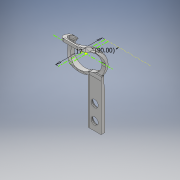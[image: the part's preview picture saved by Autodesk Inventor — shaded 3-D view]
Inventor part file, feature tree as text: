
AUTODESK INVENTOR PART (.ipt)
format: ipt  version: 2018 (Build 220112000, 112)  size: 5,239,808 bytes
history: native  units: mm
features: sketch x154, extrude x143, fillet x57, hole x4, direct_edit x3, mirror x3, other x3
ambient origin geometry x8: Origin, YZ Plane, XZ Plane, XY Plane, X Axis, Y Axis, Z Axis, Center Point
bodies: Solid2 (feature_tree)
feature tree (367):
  extrude  "Extrusion15"  Depth=18.0mm
  extrude  "Extrusion16"  Depth=1.0mm TaperAngle=0.0deg
  sketch  "Sketch28"  dims[d118=18.7mm d119=0.0mm d120=0.9mm d121=0.0mm]
  extrude  "Extrusion21"  Depth=0.9mm TaperAngle=0.0deg
  extrude  "Extrusion22"  Depth=3.467mm
  extrude  "Extrusion23"  Depth=46.7mm
  hole  "Hole6"  [1 undecoded]
  extrude  "Extrusion27"  Depth=3.467mm
  extrude  "Extrusion28"  Depth=32.03mm
  extrude  "Extrusion30"  Depth=10.0mm TaperAngle=0.0deg
  extrude  "Extrusion31"  Depth=10.0mm
  direct_edit  "Direct Edit1"
  sketch  "Sketch56"  dims[d186=16.3mm d187=0.0mm d188=16.3mm d189=0.0mm]
  sketch  "Sketch57"  dims[d190=16.3mm d191=0.0mm d192=16.3mm d193=0.0mm]
  extrude  "Extrusion33"  Depth=16.3mm TaperAngle=0.0deg
  extrude  "Extrusion34"  Depth=16.3mm TaperAngle=0.0deg
  extrude  "Extrusion35"  Depth=15.9mm TaperAngle=0.0deg
  extrude  "Extrusion36"  Depth=15.9mm TaperAngle=0.0deg
  extrude  "Extrusion37"  Depth=17.0mm
  extrude  "Extrusion38"  Depth=6.0mm TaperAngle=0.0deg
  extrude  "Extrusion39"  Depth=6.0mm TaperAngle=0.0deg
  extrude  "Extrusion40"  Depth=3.17mm
  extrude  "Extrusion41"  Depth=19.4mm
  sketch  "Sketch68"  dims[d249=0.0mm d250=0.0mm d251=10.0mm d252=0.0mm]
  sketch  "Sketch69"  dims[d253=3.91mm d254=0.0mm d255=0.0mm d256=0.0mm]
  extrude  "Extrusion42"  Depth=0.8mm TaperAngle=0.0deg
  extrude  "Extrusion43"  Depth=10.0mm
  extrude  "Extrusion45"  Depth=10.0mm TaperAngle=0.0deg
  extrude  "Extrusion47"  TaperAngle=0.0deg  [1 undecoded]
  extrude  "Extrusion48"  Depth=10.0mm TaperAngle=0.0deg
  extrude  "Extrusion49"  Depth=0.6mm TaperAngle=0.0deg
  direct_edit  "Direct Edit3"
  extrude  "Extrusion51"  Depth=0.199mm
  extrude  "Extrusion52"  TaperAngle=0.0deg  [1 undecoded]
  extrude  "Extrusion53"  Depth=0.7mm TaperAngle=0.0deg
  extrude  "Extrusion54"  Depth=3.64mm
  extrude  "Extrusion55"  Depth=0.09mm TaperAngle=0.0deg
  extrude  "Extrusion57"  Depth=0.356mm
  extrude  "Extrusion60"  Depth=3.9mm TaperAngle=0.0deg
  extrude  "Extrusion61"  Depth=3.9mm TaperAngle=0.0deg
  extrude  "Extrusion62"  Depth=0.886mm
  fillet  "Fillet13"  Radius=3.9mm
  extrude  "Extrusion63"  Depth=10.0mm TaperAngle=0.0deg
  extrude  "Extrusion64"  TaperAngle=0.0deg  [1 undecoded]
  extrude  "Extrusion65"  TaperAngle=0.0deg  [1 undecoded]
  extrude  "Extrusion66"  Depth=0.253mm
  extrude  "Extrusion67"  TaperAngle=0.0deg  [1 undecoded]
  fillet  "Fillet14"  [1 undecoded]
  extrude  "Extrusion68"  Depth=15.0mm
  extrude  "Extrusion69"  Depth=22.68928mm
  extrude  "Extrusion70"  TaperAngle=90.0deg  [1 undecoded]
  fillet  "Fillet15"  [1 undecoded]
  extrude  "Extrusion71"  Depth=0.954mm
  extrude  "Extrusion72"  Depth=3.490659mm
  extrude  "Extrusion73"  Depth=6.0mm TaperAngle=0.0deg
  extrude  "Extrusion74"  Depth=2.0mm TaperAngle=0.0deg
  fillet  "Fillet16"  Radius=2.0mm
  fillet  "Fillet17"  [1 undecoded]
  extrude  "Extrusion75"  Depth=10.0mm
  extrude  "Extrusion77"  Depth=5.0mm TaperAngle=0.0deg
  extrude  "Extrusion78"  Depth=3.8mm
  extrude  "Extrusion79"  Depth=3.213mm
  extrude  "Extrusion80"  Depth=10.0mm TaperAngle=0.0deg
  extrude  "Extrusion81"  Depth=10.0mm TaperAngle=0.0deg
  extrude  "Extrusion82"  Depth=10.0mm TaperAngle=0.0deg
  fillet  "Fillet18"  Radius=10.0mm
  fillet  "Fillet19"  Radius=10.0mm
  fillet  "Fillet20"  Radius=10.0mm
  extrude  "Extrusion83"  Depth=10.0mm TaperAngle=0.0deg
  extrude  "Extrusion84"  TaperAngle=0.0deg  [1 undecoded]
  extrude  "Extrusion85"  Depth=1.49mm
  fillet  "Fillet21"  Radius=0.859mm
  extrude  "Extrusion87"  Depth=0.149mm
  extrude  "Extrusion88"  Depth=1.77mm
  extrude  "Extrusion89"  Depth=10.0mm TaperAngle=0.0deg
  direct_edit  "Direct Edit7"
  extrude  "Extrusion90"  Depth=4.0mm TaperAngle=0.0deg
  extrude  "Extrusion91"  TaperAngle=0.0deg  [1 undecoded]
  fillet  "Fillet27"  [1 undecoded]
  extrude  "Extrusion92"  Depth=7.0mm TaperAngle=0.0deg
  extrude  "Extrusion93"  Depth=10.0mm TaperAngle=0.0deg
  extrude  "Extrusion94"  Depth=7.0mm TaperAngle=0.0deg
  fillet  "Fillet29"  Radius=7.0mm
  hole  "Hole7"  [1 undecoded]
  extrude  "Extrusion95"  Depth=1.7mm TaperAngle=0.0deg
  extrude  "Extrusion97"  Depth=8.713mm
  extrude  "Extrusion98"  Depth=2.6mm
  extrude  "Extrusion99"  TaperAngle=0.0deg  [1 undecoded]
  extrude  "Extrusion100"  Depth=10.0mm TaperAngle=0.0deg
  extrude  "Extrusion101"  Depth=10.0mm TaperAngle=0.0deg
  extrude  "Extrusion102"  TaperAngle=0.0deg  [1 undecoded]
  extrude  "Extrusion103"  Depth=10.0mm TaperAngle=0.0deg
  extrude  "Extrusion104"  TaperAngle=0.0deg  [1 undecoded]
  extrude  "Extrusion105"  Depth=1.64mm
  fillet  "Fillet30"  Radius=0.5mm
  extrude  "Extrusion106"  TaperAngle=0.0deg  [1 undecoded]
  fillet  "Fillet33"  Radius=1.2mm
  fillet  "Fillet34"  Radius=1.2mm
  fillet  "Fillet35"  Radius=1.29mm
  extrude  "Extrusion107"  Depth=10.0mm TaperAngle=0.0deg
  fillet  "Fillet36"  Radius=4.668mm
  fillet  "Fillet37"  Radius=1.4mm
  fillet  "Fillet38"  Radius=25.3mm
  extrude  "Extrusion108"  TaperAngle=0.0deg  [1 undecoded]
  extrude  "Extrusion109"  Depth=25.3mm TaperAngle=0.0deg
  extrude  "Extrusion110"  Depth=0.25mm TaperAngle=0.0deg
  extrude  "Extrusion111"  Depth=2.0mm
  extrude  "Extrusion112"  Depth=2.01mm
  sketch  "Sketch146"  dims[d552=0.25mm d553=0.0mm d554=1.4mm d555=0.0mm]
  extrude  "Extrusion113"  Depth=1.4mm TaperAngle=0.0deg
  extrude  "Extrusion114"  Depth=2.0mm
  extrude  "Extrusion115"  Depth=6.2mm TaperAngle=0.0deg
  extrude  "Extrusion116"  Depth=2.0mm
  extrude  "Extrusion118"  Depth=6.2mm TaperAngle=0.0deg
  sketch  "Sketch154"  dims[d573=5.5mm d574=2.334mm]
  extrude  "Extrusion119"  Depth=2.6mm
  extrude  "Extrusion120"  Depth=2.334mm
  extrude  "Extrusion121"  Depth=3.213mm
  extrude  "Extrusion122"  Depth=10.0mm TaperAngle=0.0deg
  extrude  "Extrusion123"  Depth=2.0mm
  extrude  "Extrusion124"  Depth=10.0mm
  extrude  "Extrusion125"  Depth=12.8mm
  extrude  "Extrusion126"  Depth=10.0mm TaperAngle=0.0deg
  extrude  "Extrusion127"  Depth=8.47mm
  hole  "Hole8"  [1 undecoded]
  extrude  "Extrusion128"  Depth=3.2mm TaperAngle=0.0deg
  extrude  "Extrusion129"  Depth=2.0mm
  extrude  "Extrusion130"  Depth=2.0mm
  extrude  "Extrusion132"  Depth=2.0mm TaperAngle=0.0deg
  extrude  "Extrusion133"  Depth=9.5mm TaperAngle=0.0deg
  extrude  "Extrusion134"  Depth=2.0mm
  extrude  "Extrusion135"  Depth=10.0mm TaperAngle=0.0deg
  extrude  "Extrusion136"  Depth=4.0mm TaperAngle=0.0deg
  extrude  "Extrusion137"  Depth=1.245mm TaperAngle=0.0deg
  extrude  "Extrusion138"  Depth=2.0mm
  extrude  "Extrusion139"  Depth=1.0mm TaperAngle=0.0deg
  extrude  "Extrusion140"  Depth=2.0mm
  sketch  "Sketch182"  dims[d641=1.33mm d642=2.0mm]
  fillet  "Fillet39"  Radius=1.0mm
  extrude  "Extrusion141"  Depth=2.0mm
  extrude  "Extrusion142"  Depth=2.0mm
  sketch  "Sketch185"  dims[d21=1.0mm d22=1.0mm]
  extrude  "Extrusion143"  Depth=2.0mm
  extrude  "Extrusion144"  Depth=2.0mm
  extrude  "Extrusion145"  Depth=1.0mm
  fillet  "Fillet41"  [1 undecoded]
  extrude  "Extrusion146"  [1 undecoded]
  extrude  "Extrusion147"  [1 undecoded]
  extrude  "Extrusion148"  [1 undecoded]
  extrude  "Extrusion149"  [1 undecoded]
  extrude  "Extrusion150"  [1 undecoded]
  extrude  "Extrusion152"  [1 undecoded]
  extrude  "Extrusion153"  [1 undecoded]
  extrude  "Extrusion154"  [1 undecoded]
  extrude  "Extrusion155"  [1 undecoded]
  fillet  "Fillet42"  [1 undecoded]
  fillet  "Fillet43"  [1 undecoded]
  fillet  "Fillet44"  [1 undecoded]
  fillet  "Fillet45"  [1 undecoded]
  extrude  "Extrusion156"  [1 undecoded]
  extrude  "Extrusion157"  [1 undecoded]
  fillet  "Fillet46"  [1 undecoded]
  fillet  "Fillet47"  [1 undecoded]
  fillet  "Fillet48"  [1 undecoded]
  extrude  "Extrusion158"  [1 undecoded]
  extrude  "Extrusion159"  [1 undecoded]
  fillet  "Fillet49"  [1 undecoded]
  extrude  "Extrusion160"  [1 undecoded]
  extrude  "Extrusion162"  [1 undecoded]
  hole  "Hole9"  [1 undecoded]
  sketch  "Sketch205"
  extrude  "Extrusion163"  [1 undecoded]
  fillet  "Fillet50"  [1 undecoded]
  fillet  "Fillet51"  [1 undecoded]
  extrude  "Extrusion164"  [1 undecoded]
  fillet  "Fillet52"  [1 undecoded]
  fillet  "Fillet53"  [1 undecoded]
  fillet  "Fillet54"  [1 undecoded]
  fillet  "Fillet55"  [1 undecoded]
  extrude  "Extrusion165"  [1 undecoded]
  fillet  "Fillet56"  [1 undecoded]
  fillet  "Fillet57"  [1 undecoded]
  extrude  "Extrusion166"  [1 undecoded]
  extrude  "Extrusion167"  [1 undecoded]
  extrude  "Extrusion168"  [1 undecoded]
  extrude  "Extrusion169"  [1 undecoded]
  fillet  "Fillet58"  [1 undecoded]
  fillet  "Fillet59"  [1 undecoded]
  fillet  "Fillet60"  [1 undecoded]
  fillet  "Fillet61"  [1 undecoded]
  fillet  "Fillet62"  [1 undecoded]
  extrude  "Extrusion170"  [1 undecoded]
  extrude  "Extrusion171"  [1 undecoded]
  extrude  "Extrusion172"  [1 undecoded]
  fillet  "Fillet63"  [1 undecoded]
  fillet  "Fillet64"  [1 undecoded]
  fillet  "Fillet65"  [1 undecoded]
  sketch  "Sketch220"
  extrude  "Extrusion173"  [1 undecoded]
  extrude  "Extrusion174"  [1 undecoded]
  extrude  "Extrusion175"  [1 undecoded]
  extrude  "Extrusion176"  [1 undecoded]
  extrude  "Extrusion177"  [1 undecoded]
  fillet  "Fillet66"  [1 undecoded]
  sketch  "Sketch225"
  fillet  "Fillet67"  [1 undecoded]
  fillet  "Fillet68"  [1 undecoded]
  extrude  "Extrusion178"  [1 undecoded]
  fillet  "Fillet69"  [1 undecoded]
  fillet  "Fillet70"  [1 undecoded]
  extrude  "Extrusion179"  [1 undecoded]
  fillet  "Fillet71"  [1 undecoded]
  fillet  "Fillet72"  [1 undecoded]
  fillet  "Fillet73"  [1 undecoded]
  fillet  "Fillet74"  [1 undecoded]
  fillet  "Fillet75"  [1 undecoded]
  fillet  "Fillet76"  [1 undecoded]
  fillet  "Fillet77"  [1 undecoded]
  fillet  "Fillet78"  [1 undecoded]
  mirror  "Mirror7"
  mirror  "Mirror8"
  mirror  "Mirror9"
  sketch  "Sketch26"  dims[d95=7.5mm d96=18.0mm]
  sketch  "Sketch27"  dims[d97=2.3mm d98=0.0mm d101=1.0mm d102=0.0mm]
  sketch  "Sketch41"  dims[d122=0.7mm d123=0.0mm d128=3.467mm]
  sketch  "Sketch42"  dims[d129=3.467mm d130=46.7mm]
  sketch  "Sketch43"  dims[d134=3.467mm d135=4.369mm d136=5.824mm d137=2.0mm d138=14.3117mm d139=6.637mm d140=0.0mm d150=1.5mm d151=0.0mm]
  sketch  "Sketch50"  dims[d152=1.2mm d153=0.0mm d159=3.467mm]
  sketch  "Sketch51"  dims[d161=3.467mm d168=23.3333mm d173=32.03mm]
  sketch  "Sketch53"  dims[d174=16.015mm d175=10.0mm d176=0.0mm]
  sketch  "Sketch54"  dims[d179=0.0mm d180=0.0mm d181=7.5mm d182=10.0mm d183=10.0mm]
  sketch  "Sketch58"  dims[d194=16.3mm d195=0.0mm d196=15.9mm d197=0.0mm]
  sketch  "Sketch60"  dims[d198=15.9mm d199=0.0mm d200=15.9mm d201=0.0mm]
  sketch  "Sketch61"  dims[d202=15.9mm d203=0.0mm d209=17.0mm]
  sketch  "Sketch62"  dims[d210=90.0deg d211=6.0mm d212=0.0mm]
  sketch  "Sketch63"  dims[d213=0.0mm d214=0.0mm d225=6.0mm d226=0.0mm]
  sketch  "Sketch64"  dims[d230=0.2mm d231=0.0mm d232=3.17mm]
  sketch  "Sketch65"  dims[d233=3.17mm d235=19.4mm]
  sketch  "Sketch66"  dims[d236=6.1mm d237=0.8mm d238=0.0mm]
  sketch  "Sketch67"  dims[d239=0.8mm d240=0.0mm d246=9.0mm d247=10.0mm d248=10.0mm]
  sketch  "Sketch70"  dims[d257=3.91mm d258=0.0mm d261=10.0mm d262=0.0mm]
  sketch  "Sketch72"  dims[d267=0.0mm d268=0.0mm d269=0.6mm d270=0.0mm]
  sketch  "Sketch74"  dims[d271=0.0mm d272=0.0mm d273=0.199mm]
  sketch  "Sketch75"  dims[d274=0.7mm d275=0.0mm d276=0.0mm d277=0.0mm]
  sketch  "Sketch76"  dims[d278=0.0mm d279=0.0mm d280=0.7mm d281=0.0mm]
  sketch  "Sketch79"  dims[d282=0.7mm d283=0.0mm d284=3.64mm]
  sketch  "Sketch80"  dims[d285=0.09mm d286=0.0mm d287=0.09mm d288=0.0mm]
  sketch  "Sketch81"  dims[d289=0.0mm d290=0.0mm d291=0.356mm]
  sketch  "Sketch82"  dims[d292=3.9mm d293=0.0mm d294=3.9mm d295=0.0mm]
  sketch  "Sketch83"  dims[d296=0.0mm d297=0.0mm d298=3.9mm d299=0.0mm]
  sketch  "Sketch86"  dims[d300=0.657mm d301=0.886mm d302=3.9mm d303=0.0mm]
  sketch  "Sketch89"  dims[d309=10.0mm d310=0.0mm d313=10.0mm d314=0.0mm]
  sketch  "Sketch90"  dims[d315=10.0mm d316=0.0mm d317=0.0mm d318=0.0mm]
  sketch  "Sketch91"  dims[d319=10.0mm d320=0.0mm d321=0.0mm d322=0.0mm]
  sketch  "Sketch92"  dims[d323=0.467mm d324=0.253mm]
  sketch  "Sketch93"  dims[d325=0.195mm d326=0.0mm d327=0.0mm d328=90.0deg]
  sketch  "Sketch94"  dims[d329=90.0deg d330=15.0mm]
  sketch  "Sketch95"  dims[d332=11.0mm d333=22.68928mm]
  sketch  "Sketch96"  dims[d335=90.0deg d336=90.0deg d337=0.0mm d338=0.0mm]
  sketch  "Sketch97"  dims[d339=15.0mm d342=7.0mm d343=0.0mm d344=0.954mm]
  sketch  "Sketch98"  dims[d350=90.0deg d351=3.490659mm]
  sketch  "Sketch99"  dims[d352=3.490659mm d353=6.0mm d354=0.0mm]
  sketch  "Sketch100"  dims[d362=1.65mm d363=2.0mm d364=0.0mm d365=2.0mm d366=0.0mm]
  sketch  "Sketch101"  dims[d371=8.5mm d372=10.0mm d373=10.0mm d374=0.0mm d375=0.0mm]
  sketch  "Sketch102"  dims[d376=10.0mm d377=0.0mm d378=0.22mm]
  sketch  "Sketch103"  dims[d379=5.1mm d380=0.0mm d381=5.0mm d382=0.0mm]
  sketch  "Sketch104"  dims[d383=5.0mm d384=0.0mm d386=3.8mm]
  sketch  "Sketch105"  dims[d387=2.6mm d388=3.213mm]
  sketch  "Sketch106"  dims[d389=2.975mm]
  sketch  "Sketch107"  dims[d390=2.6mm d391=6.0mm d392=4.4mm d393=2.0mm d394=14.3117mm d395=8.0mm d396=20.594885mm d397=10.0mm d398=0.0mm]
  sketch  "Sketch108"  dims[d401=0.3mm d402=0.0mm d403=10.0mm d404=0.0mm]
  sketch  "Sketch109"  dims[d405=10.0mm d406=0.0mm d407=10.0mm d408=0.0mm d409=10.0mm d410=0.0mm d411=10.0mm d412=0.0mm d413=10.0mm d414=0.0mm]
  sketch  "Sketch110"  dims[d415=10.0mm d416=0.0mm d417=1.0mm d418=0.0mm]
  sketch  "Sketch113"  dims[d419=0.865mm d421=0.0mm d422=0.0mm]
  sketch  "Sketch114"  dims[d424=5.99mm d425=1.49mm d426=0.859mm]
  sketch  "Sketch115"  dims[d427=1.0mm d428=0.0mm d429=0.149mm]
  sketch  "Sketch117"  dims[d430=0.346mm d431=1.77mm]
  sketch  "Sketch118"  dims[d432=10.0mm d433=0.0mm d434=4.0mm d435=0.0mm]
  sketch  "Sketch119"  dims[d436=4.0mm d437=0.0mm d438=4.0mm d439=0.0mm]
  sketch  "Sketch120"  dims[d440=4.0mm d441=0.0mm d442=0.0mm d443=0.0mm d444=0.0mm d445=0.0mm]
  sketch  "Sketch121"  dims[d446=1.0mm d447=0.0mm d448=7.0mm d449=0.0mm]
  sketch  "Sketch122"  dims[d452=7.0mm d453=0.0mm d454=10.0mm d455=0.0mm]
  sketch  "Sketch123"  dims[d456=0.0mm d457=0.0mm d458=7.0mm d459=0.0mm d460=7.0mm d461=0.0mm]
  sketch  "Sketch124"  dims[d462=0.0mm d463=0.0mm d464=7.0mm d465=0.0mm]
  sketch  "Sketch125"  dims[d466=1.7mm d467=0.0mm d468=1.7mm d469=0.0mm]
  sketch  "Sketch126"  dims[d470=5.95mm d471=8.713mm]
  sketch  "Sketch128"  dims[d472=1.403mm d473=0.0mm d474=2.6mm]
  sketch  "Sketch129"  dims[d475=5.5mm]
  sketch  "Sketch130"  dims[d476=2.6mm d477=6.0mm d478=4.4mm d479=2.0mm d480=14.3117mm d481=8.0mm d482=20.594885mm d483=0.0mm d484=0.0mm]
  sketch  "Sketch131"  dims[d485=0.0mm d486=0.0mm d487=10.0mm d488=0.0mm]
  sketch  "Sketch132"  dims[d494=10.0mm d495=0.0mm d496=10.0mm d497=0.0mm]
  sketch  "Sketch133"  dims[d498=10.0mm d499=0.0mm d500=0.0mm d501=0.0mm]
  sketch  "Sketch134"  dims[d502=10.0mm d503=0.0mm d504=3.7mm d505=0.0mm]
  sketch  "Sketch135"  dims[d506=3.7mm d507=0.0mm d508=0.0mm d509=0.0mm]
  sketch  "Sketch136"  dims[d510=0.0mm d511=0.0mm d512=1.64mm d513=0.5mm d514=0.0mm]
  sketch  "Sketch137"  dims[d515=5.0mm d516=0.0mm d517=0.0mm d518=0.0mm d519=1.2mm d520=0.0mm d521=1.2mm d522=0.0mm d524=1.29mm]
  sketch  "Sketch140"  dims[d525=0.0mm d526=0.0mm d527=10.0mm d528=0.0mm d529=4.668mm d530=1.4mm d531=25.3mm d532=0.0mm]
  sketch  "Sketch141"  dims[d533=25.3mm d534=0.0mm d535=0.0mm d536=0.0mm]
  sketch  "Sketch142"  dims[d539=0.0mm d540=0.0mm d541=25.3mm d542=0.0mm]
  sketch  "Sketch143"  dims[d544=0.4mm d545=0.0mm d546=0.25mm d547=0.0mm]
  sketch  "Sketch144"  dims[d548=2.0mm d549=2.0mm]
  sketch  "Sketch145"  dims[d550=2.8mm d551=2.01mm]
  sketch  "Sketch147"  dims[d556=2.0mm d557=2.0mm]
  sketch  "Sketch148"  dims[d558=3.52mm d559=6.2mm d560=0.0mm]
  sketch  "Sketch149"  dims[d561=6.2mm d562=0.0mm d563=2.0mm]
  sketch  "Sketch150"  dims[d564=7.35mm d565=0.0mm d568=6.2mm d569=0.0mm]
  sketch  "Sketch153"  dims[d570=2.6mm d571=2.6mm]
  sketch  "Sketch156"  dims[d575=2.334mm d576=3.213mm]
  sketch  "Sketch157"  dims[d577=2.6mm d578=6.0mm d579=4.4mm d580=2.0mm d581=14.3117mm d582=8.0mm d583=20.594885mm d584=10.0mm d585=0.0mm]
  sketch  "Sketch161"  dims[d586=2.0mm d587=2.28mm]
  sketch  "Sketch162"  dims[d588=10.0mm d589=0.0mm d590=3.95mm]
  sketch  "Sketch163"  dims[d591=9.98mm d592=12.8mm]
  sketch  "Sketch164"  dims[d593=68.9mm d594=10.0mm d595=0.0mm]
  sketch  "Sketch165"  dims[d596=4.18mm d597=8.47mm]
  sketch  "Sketch166"  dims[d598=10.0mm d599=0.0mm d600=3.2mm d601=0.0mm]
  sketch  "Sketch168"  dims[d602=0.0mm d603=0.0mm d604=3.2mm d605=0.0mm]
  sketch  "Sketch169"  dims[d606=2.0mm d607=2.0mm]
  sketch  "Sketch170"  dims[d608=2.0mm d609=2.0mm]
  sketch  "Sketch171"  dims[d610=2.0mm d611=3.2mm d612=0.0mm]
  sketch  "Sketch173"  dims[d613=9.5mm d614=0.0mm d615=9.5mm d616=0.0mm]
  sketch  "Sketch174"  dims[d617=2.0mm d618=2.0mm]
  sketch  "Sketch175"  dims[d619=2.0mm d620=10.0mm d621=0.0mm]
  sketch  "Sketch176"  dims[d622=4.0mm d623=0.0mm d624=4.0mm d625=0.0mm]
  sketch  "Sketch177"  dims[d626=4.0mm d627=0.0mm d628=1.245mm d629=0.0mm]
  sketch  "Sketch178"  dims[d630=2.0mm d631=0.15mm]
  sketch  "Sketch179"  dims[d632=0.279mm d633=1.0mm d634=0.0mm]
  sketch  "Sketch180"  dims[d635=2.0mm d636=2.0mm d637=1.0mm d638=0.0mm]
  sketch  "Sketch181"  dims[d639=2.0mm d640=1.24mm]
  sketch  "Sketch183"  dims[d643=2.0mm d644=2.0mm]
  sketch  "Sketch184"  dims[d645=2.0mm d646=2.0mm]
  sketch  "Sketch186"
  sketch  "Sketch187"
  sketch  "Sketch188"
  sketch  "Sketch189"
  sketch  "Sketch190"
  sketch  "Sketch191"
  sketch  "Sketch192"
  sketch  "Sketch193"
  sketch  "Sketch194"
  sketch  "Sketch195"
  sketch  "Sketch196"
  sketch  "Sketch197"
  sketch  "Sketch199"
  sketch  "Sketch200"
  sketch  "Sketch201"
  sketch  "Sketch202"
  sketch  "Sketch203"
  sketch  "Sketch204"
  sketch  "Sketch207"
  sketch  "Sketch208"
  sketch  "Sketch209"
  sketch  "Sketch210"
  sketch  "Sketch211"
  sketch  "Sketch212"
  sketch  "Sketch213"
  sketch  "Sketch216"
  sketch  "Sketch217"
  sketch  "Sketch218"
  sketch  "Sketch221"
  sketch  "Sketch222"
  sketch  "Sketch223"
  sketch  "Sketch224"
  sketch  "Sketch226"
  sketch  "Sketch227"
  other  "Scale1"
  other  "Scale3"
  other  "Scale7"
note: 91 required parameter values undecoded (feature->parameter linkage not recoverable at this tier; creation-order binding heuristic only, values carry confidence <= 0.55)
